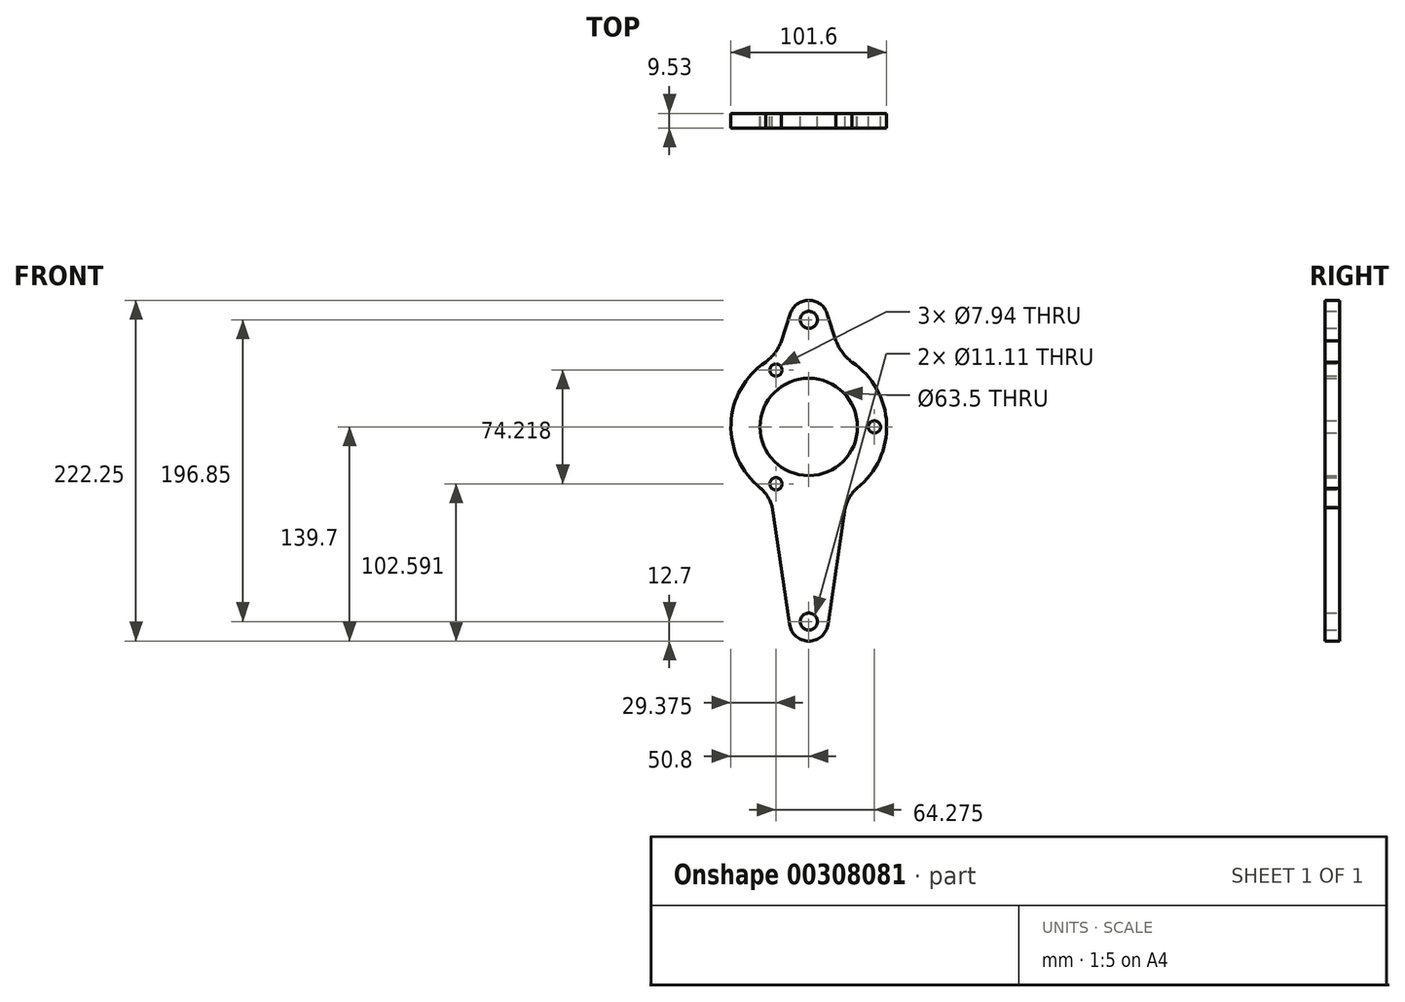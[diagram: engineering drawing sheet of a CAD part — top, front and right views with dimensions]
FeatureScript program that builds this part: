
annotation { "Feature Type Name" : "Feature", "Feature Type Description" : "" }
export const myFeature = defineFeature(function(context is Context, id is Id, definition is map)
    precondition{}
    {
        {
            var Q0;
            Q0=qCreatedBy(makeId("Front.planeOp"),FACE);
            var sketch = newSketch(context, id + "F0", { "sketchPlane" : qUnion([Q0])});
            skArc(sketch, "E0", {"start": v(31.44, -39.9) * mm, "mid": v(50.76, 2) * mm, "end": v(28.19, 42.26) * mm});
            skCircle(sketch, "E1", {"center": v(0, 0) * mm, "radius": 31.75 * mm});
            skLineSegment(sketch, "E2", {"start": v(0, 117.02) * mm, "end": v(0, -168.81) * mm, "construction": true});
            skLineSegment(sketch, "E3", {"start": v(-75.94, 0) * mm, "end": v(123.61, 0) * mm, "construction": true});
            skCircle(sketch, "E4", {"center": v(0, 69.85) * mm, "radius": 5.56 * mm});
            skCircle(sketch, "E5", {"center": v(0, -127) * mm, "radius": 5.56 * mm});
            skArc(sketch, "E6", {"start": v(12.08, 73.76) * mm, "mid": v(0, 82.55) * mm, "end": v(-12.08, 73.77) * mm});
            skArc(sketch, "E7", {"start": v(-12.56, -128.88) * mm, "mid": v(0, -139.7) * mm, "end": v(12.56, -128.86) * mm});
            skCircle(sketch, "E8", {"center": v(-21.42, 37.1) * mm, "radius": 3.97 * mm});
            skCircle(sketch, "E9", {"center": v(-21.42, -37.1) * mm, "radius": 3.97 * mm});
            skLineSegment(sketch, "E10", {"start": v(-24.08, -51.75) * mm, "end": v(-12.56, -128.88) * mm});
            skLineSegment(sketch, "E11", {"start": v(23.81, -52.8) * mm, "end": v(12.56, -128.86) * mm});
            skArc(sketch, "E12", {"start": v(33.1, -38.54) * mm, "mid": v(26.16, -46.6) * mm, "end": v(23.22, -56.83) * mm});
            skArc(sketch, "E13.MirrorCS", {"start": v(-33.1, -38.54) * mm, "mid": v(-26.16, -46.6) * mm, "end": v(-23.22, -56.83) * mm});
            skLineSegment(sketch, "E14", {"start": v(-17.88, 55.9) * mm, "end": v(-12.08, 73.77) * mm});
            skLineSegment(sketch, "E15", {"start": v(17.78, 56.17) * mm, "end": v(12.08, 73.76) * mm});
            skArc(sketch, "E16", {"start": v(16.98, 58.65) * mm, "mid": v(21.81, 48.7) * mm, "end": v(29.86, 41.1) * mm});
            skArc(sketch, "E17.MirrorCS", {"start": v(-16.98, 58.65) * mm, "mid": v(-21.81, 48.7) * mm, "end": v(-29.86, 41.1) * mm});
            skArc(sketch, "E18.trimOffspring", {"start": v(-28.19, 42.26) * mm, "mid": v(-50.76, 2) * mm, "end": v(-31.44, -39.9) * mm});
            skCircle(sketch, "E19", {"center": v(42.85, 0) * mm, "radius": 3.97 * mm});
            skSolve(sketch);
        }
        {
            var Q0;
            Q0 = qSketchRegion(id + "F0", true);
            extrude(context, id + "F1", {"entities" : qUnion([Q0]), "depth" : 9.52 * mm, "offsetDistance" : 25.4 * mm});
        }
    });
